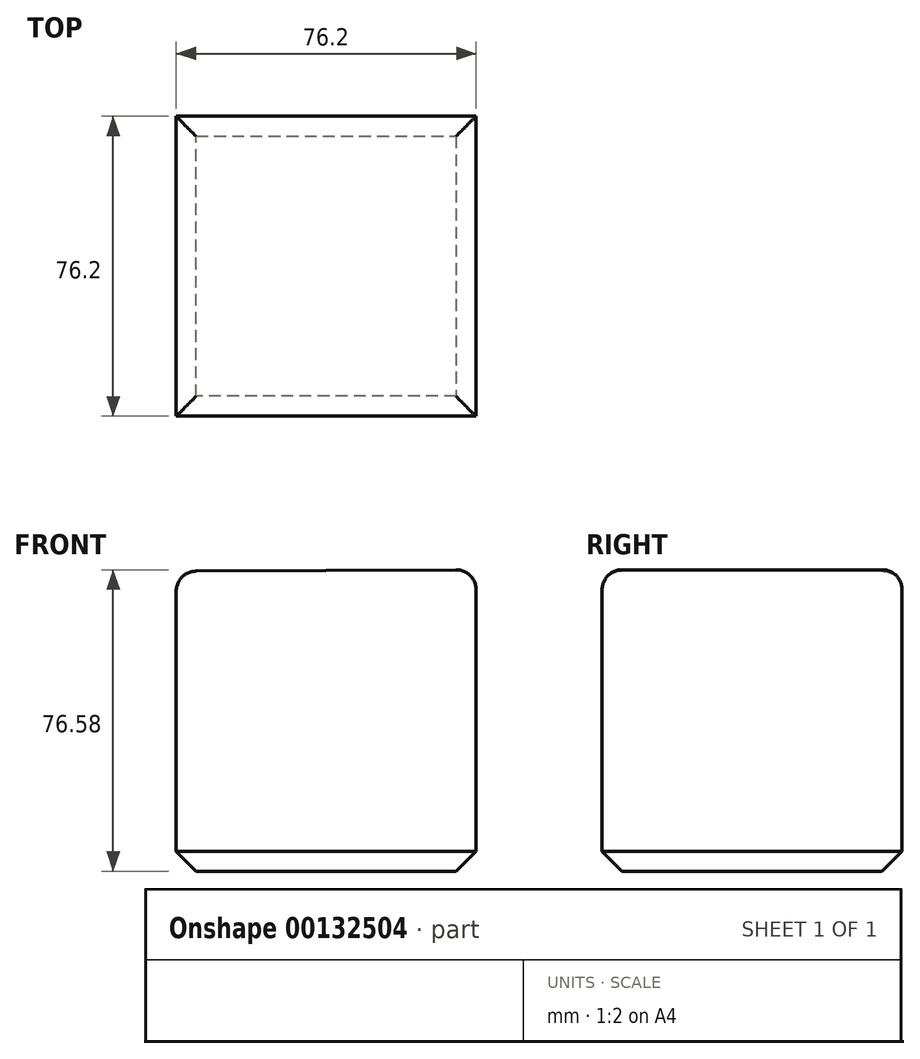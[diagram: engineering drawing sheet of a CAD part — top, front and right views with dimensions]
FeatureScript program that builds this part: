
annotation { "Feature Type Name" : "Feature", "Feature Type Description" : "" }
export const myFeature = defineFeature(function(context is Context, id is Id, definition is map)
    precondition{}
    {
        {
            var Q0;
            Q0=qCreatedBy(makeId("Front.planeOp"),FACE);
            var sketch = newSketch(context, id + "F0", { "sketchPlane" : qUnion([Q0])});
            skLineSegment(sketch, "E0", {"start": v(-76.2, 76.2) * mm, "end": v(-76.2, 0) * mm});
            skLineSegment(sketch, "E1", {"start": v(-76.2, 0) * mm, "end": v(0, 0) * mm});
            skLineSegment(sketch, "E2", {"start": v(0, 0) * mm, "end": v(0, 76.6) * mm});
            skLineSegment(sketch, "E3", {"start": v(-76.2, 76.2) * mm, "end": v(0, 76.6) * mm});
            skSolve(sketch);
        }
        {
            var Q0;
            Q0 = qSketchRegion(id + "F0", true);
            extrude(context, id + "F1", {"entities" : qUnion([Q0]), "depth" : 76.2 * mm});
        }
        {
            var Q0;
            Q0=makeQuery(id+"F1.opExtrude","CAP_EDGE",EDGE,{"disambiguationData":[OSD([sQuery(id+"F0.wireOp",EDGE,"E3")])],"isStart":true});
            var Q1;
            Q1=makeQuery(id+"F1.opExtrude","SWEPT_EDGE",EDGE,{"disambiguationData":[OSD([sQuery(id+"F0.wireOp",EDGE,"E0"),sQuery(id+"F0.wireOp",EDGE,"E3")])]});
            var Q2;
            Q2=makeQuery(id+"F1.opExtrude","SWEPT_EDGE",EDGE,{"disambiguationData":[OSD([sQuery(id+"F0.wireOp",EDGE,"E2"),sQuery(id+"F0.wireOp",EDGE,"E3")])]});
            var Q3;
            Q3=makeQuery(id+"F1.opExtrude","CAP_EDGE",EDGE,{"disambiguationData":[OSD([sQuery(id+"F0.wireOp",EDGE,"E3")])],"isStart":false});
            fillet(context, id + "F2", {"entities" : qUnion([Q0, Q1, Q2, Q3]), "radius" : 5.08 * mm, "tangentPropagation" : true, "allowEdgeOverflow" : false});
        }
        {
            var Q0;
            Q0=makeQuery(id+"F1.opExtrude","SWEPT_EDGE",EDGE,{"disambiguationData":[OSD([sQuery(id+"F0.wireOp",EDGE,"E0"),sQuery(id+"F0.wireOp",EDGE,"E1")])]});
            var Q1;
            Q1=makeQuery(id+"F1.opExtrude","CAP_EDGE",EDGE,{"disambiguationData":[OSD([sQuery(id+"F0.wireOp",EDGE,"E1")])],"isStart":false});
            var Q2;
            Q2=makeQuery(id+"F1.opExtrude","SWEPT_EDGE",EDGE,{"disambiguationData":[OSD([sQuery(id+"F0.wireOp",EDGE,"E1"),sQuery(id+"F0.wireOp",EDGE,"E2")])]});
            var Q3;
            Q3=makeQuery(id+"F1.opExtrude","CAP_EDGE",EDGE,{"disambiguationData":[OSD([sQuery(id+"F0.wireOp",EDGE,"E1")])],"isStart":true});
            chamfer(context, id + "F3", {"entities" : qUnion([Q0, Q1, Q2, Q3]), "width" : 5.08 * mm, "tangentPropagation" : true});
        }
    });
